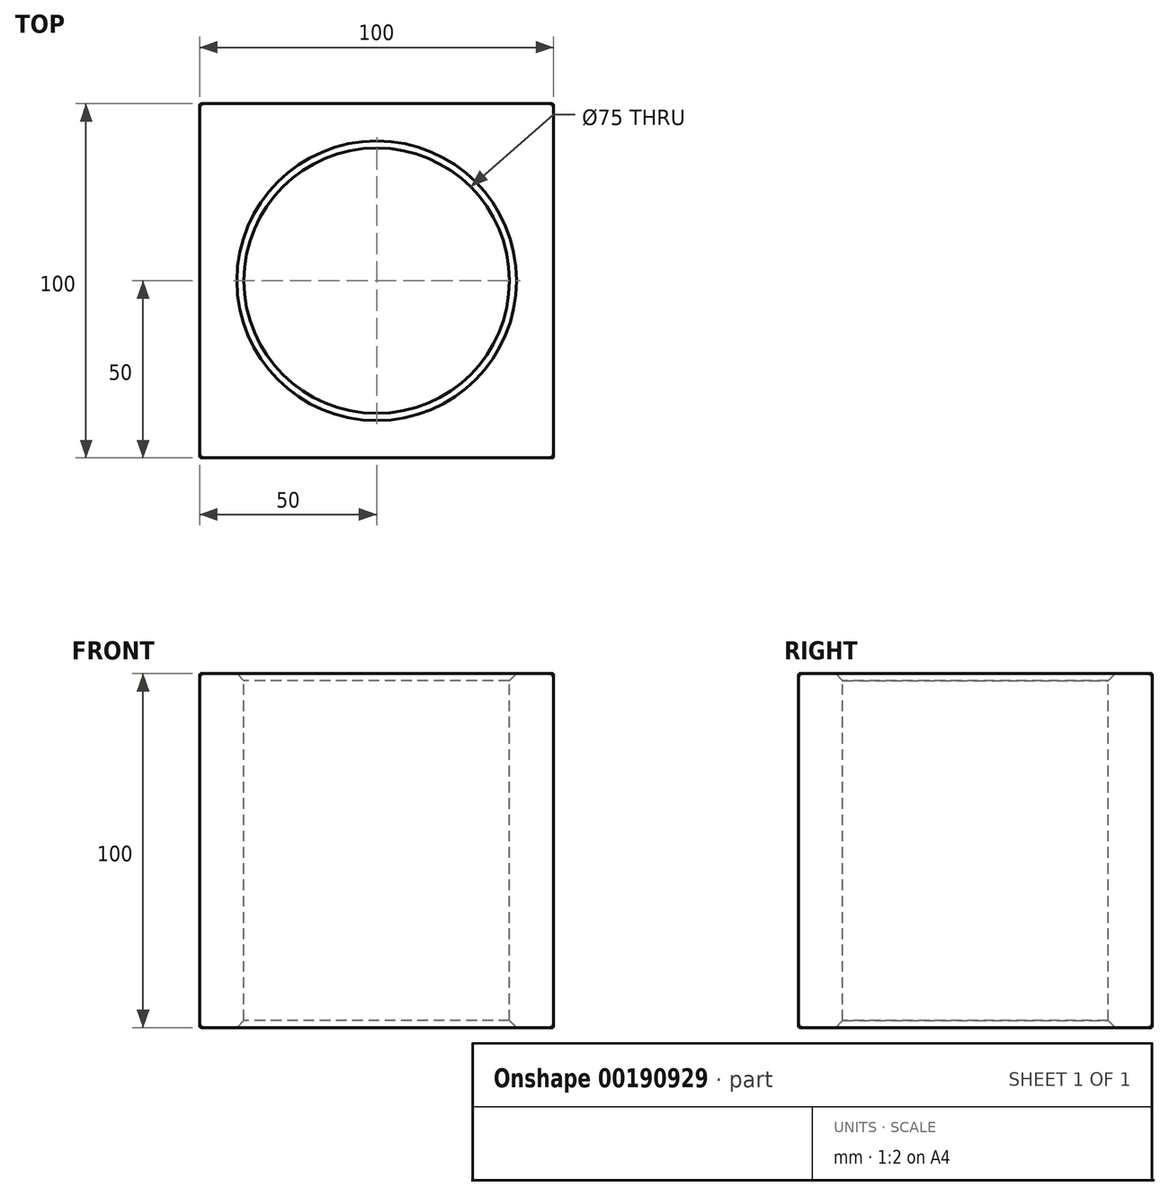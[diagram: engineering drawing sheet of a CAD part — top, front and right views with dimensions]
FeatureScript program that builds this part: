
annotation { "Feature Type Name" : "Feature", "Feature Type Description" : "" }
export const myFeature = defineFeature(function(context is Context, id is Id, definition is map)
    precondition{}
    {
        {
            var Q0;
            Q0=qCreatedBy(makeId("Top.planeOp"),FACE);
            var sketch = newSketch(context, id + "F0", { "sketchPlane" : qUnion([Q0])});
            skLineSegment(sketch, "E0.bottom", {"start": v(50, 50) * mm, "end": v(-50, 50) * mm});
            skLineSegment(sketch, "E0.top", {"start": v(50, -50) * mm, "end": v(-50, -50) * mm});
            skLineSegment(sketch, "E0.left", {"start": v(50, 50) * mm, "end": v(50, -50) * mm});
            skLineSegment(sketch, "E0.right", {"start": v(-50, 50) * mm, "end": v(-50, -50) * mm});
            skPoint(sketch, "E0.middle", {"position": v(0, 0) * mm});
            skSolve(sketch);
        }
        {
            var Q0;
            Q0 = qSketchRegion(id + "F0", true);
            extrude(context, id + "F1", {"entities" : qUnion([Q0]), "depth" : 100 * mm, "offsetDistance" : 25 * mm, "symmetric" : true});
        }
        {
            var Q0;
            Q0=makeQuery(id+"F1.opExtrude","CAP_FACE",FACE,{"disambiguationData":[OSD([sQuery(id+"F0.wireOp",EDGE,"E0.bottom"),sQuery(id+"F0.wireOp",EDGE,"E0.top"),sQuery(id+"F0.wireOp",EDGE,"E0.left"),sQuery(id+"F0.wireOp",EDGE,"E0.right")])],"isStart":false});
            var sketch = newSketch(context, id + "F2", { "sketchPlane" : qUnion([Q0])});
            skCircle(sketch, "E1", {"center": v(0, 0) * mm, "radius": 37.5 * mm});
            skSolve(sketch);
        }
        {
            var Q0;
            Q0 = qSketchRegion(id + "F2", true);
            extrude(context, id + "F3", {"entities" : qUnion([Q0]), "operationType" : NewBodyOperationType.REMOVE, "endBound" : BoundingType.THROUGH_ALL, "oppositeDirection" : true, "depth" : 25 * mm, "offsetDistance" : 25 * mm});
        }
        {
            var Q0;
            Q0=makeQuery(id+"F3.boolean.opBoolean","COPY",FACE,{"derivedFrom":makeQuery(id+"F3.opExtrude","SWEPT_FACE",FACE,{"disambiguationData":[OSD([sQuery(id+"F2.wireOp",EDGE,"E1")])]})});
            chamfer(context, id + "F4", {"entities" : qUnion([Q0]), "width" : 2 * mm, "tangentPropagation" : true});
        }
        {
            var Q0;
            Q0=makeQuery(id+"F1.opExtrude","SWEPT_FACE",FACE,{"disambiguationData":[OSD([sQuery(id+"F0.wireOp",EDGE,"E0.top")])]});
            var Q1;
            Q1=makeQuery(id+"F1.opExtrude","SWEPT_FACE",FACE,{"disambiguationData":[OSD([sQuery(id+"F0.wireOp",EDGE,"E0.bottom")])]});
            var Q2;
            Q2=makeQuery(id+"F1.opExtrude","SWEPT_FACE",FACE,{"disambiguationData":[OSD([sQuery(id+"F0.wireOp",EDGE,"E0.left")])]});
            var Q3;
            Q3=makeQuery(id+"F1.opExtrude","SWEPT_FACE",FACE,{"disambiguationData":[OSD([sQuery(id+"F0.wireOp",EDGE,"E0.right")])]});
            fillet(context, id + "F5", {"entities" : qUnion([Q0, Q1, Q2, Q3]), "radius" : 0.5 * mm, "tangentPropagation" : true, "rho" : 0.5, "crossSection" : FilletCrossSection.CONIC, "allowEdgeOverflow" : false});
        }
    });
